# Revit family: Grohe_PlumbingFixture_Lineare_BasinMixer_23106001a
name_source: partatom
category: Plumbing Fixtures
revit_build: Autodesk Revit 2018 (Build: 20190510_1515(x64)
units: mm (PartAtom-declared; Revit-internal decimal feet)

## family parameters
Cut with Voids When Loaded = No
Host = Face
OmniClass Number = 23.65.00.00
OmniClass Title = Supply and Distribution of Liquids and Gases
Part Type = Normal
Room Calculation Point = No
Round Connector Dimension = Use Diameter
Shared = No

## types (1)
- 23106001
    ADACompliant = No
    Assembly Code = D2020300
    BIMObjectName = Grohe_PlumbingFixture_Lineare_BasinMixer_23106001
    CWFU = 4.5
    ClassificationName = Uniclass 2015
    ClassificationValue = Pr_40_20_87_98
    ColdWaterConnectionDiameter = 10 mm  [stored 0.0328084 ft]
    Color = Chrome
    Default Elevation = 0 mm  [stored 0 ft]
    Description = Minimalist design meets innovative technology! With its smooth cylindrical body and crisp rectangular handle and spout the GROHE Lineare single-lever basin mixer looks perfect in any contemporary bathroom. A delight to use, it has a fingertip operated pop-open waste and is packed with GROHE technology. The control of water volume and temperature is precise and effortless thanks to the GROHE SilkMove ceramic cartridge while the GROHE EcoJoy feature limits water usage to 5.7 l/m – delivering a satisfying flow but saving water and money. The gleaming GROHE StarLight chrome coating is scratch-resistant and needs only a wipe with a dry cloth to look as good as new. It’s easy to install, too, as the GROHE QuickFix Plus system cuts fitting time by up to 50%! An instant bathroom upgrade that balances harmonious style with performance you can trust!
    DocumentationCertificates = https://www.bimstore.co
    DocumentationInstallationGuide = https://www.bimstore.co
    DocumentationLiterature = https://www.bimstore.co
    DocumentationMaintenance = https://www.bimstore.co
    DocumentationTechnical = https://www.bimstore.co
    DurationUnit = Years
    Ecojoy = No
    ExpectedLife = 0
    Features = Minimalist design meets innovative technology! With its smooth cylindrical body and crisp rectangular handle and spout the GROHE Lineare single-lever basin mixer looks perfect in any contemporary bathroom. A delight to use, it has a fingertip operated pop-open waste and is packed with GROHE technology. The control of water volume and temperature is precise and effortless thanks to the GROHE SilkMove ceramic cartridge while the GROHE EcoJoy feature limits water usage to 5.7 l/m – delivering a satisfying flow but saving water and money. The gleaming GROHE StarLight chrome coating is scratch-resistant and needs only a wipe with a dry cloth to look as good as new. It’s easy to install, too, as the GROHE QuickFix Plus system cuts fitting time by up to 50%! An instant bathroom upgrade that balances harmonious style with performance you can trust!
    HWFU = 4.5
    HotWaterConnectionDiameter = 10 mm  [stored 0.0328084 ft]
    IfcExportAs = IfcPipeFitting
    IfcExportType = IfcPipeFittingType
    Keynote = N13
    LowEmittingMaterial = No
    Manufacturer = Grohe
    ManufacturerName = Grohe
    MasterformatNumber = 01 52 19
    MasterformatTitle = Sanitary Facilities
    Model = Lineare - Basin mixer 1/2″ S-Size
    ModelNumber = 23106001
    ModelReference = Lineare - Basin mixer 1/2″ S-Size
    NBSDescription = Water supply fittings for wash basins and troughs
    NBSObjectName = Grohe - Water supply fittings for wash basins and troughs
    NBSReference = 45-35-70/371
    NominalDepth = 0 mm  [stored 0 ft]
    NominalHeight = 0 mm  [stored 0 ft]
    NominalLength = 0 mm  [stored 0 ft]
    PrimaryMaterial = Steel, Chrome Plated
    ProductDocumentationLink = https://www.grohe.co.uk
    ProductPageURL = https://www.grohe.co.uk
    ProductionYear = 2020
    Type Comments = 23106001
    TypeName = Lineare - Basin mixer 1/2″ S-Size
    URL = https://www.grohe.co.uk
    WarrantyDurationLabor = 0
    WarrantyDurationParts = 0
    WarrantyDurationUnit = Years
    _BSBibleVersion = 16
    _BimSpecGuid = 0
    _CurrentRevision = 1
    _DistributedBy = www.bimstore.co
    _ObjectUserGuide = https://www.bimstore.co

note: [stored X ft] marks values corroborated as IEEE doubles in the binary element streams (Revit-internal decimal feet)

## geometry (parser evidence)
native form markers: Sweep x2
no freeform markers — native parametric forms only
